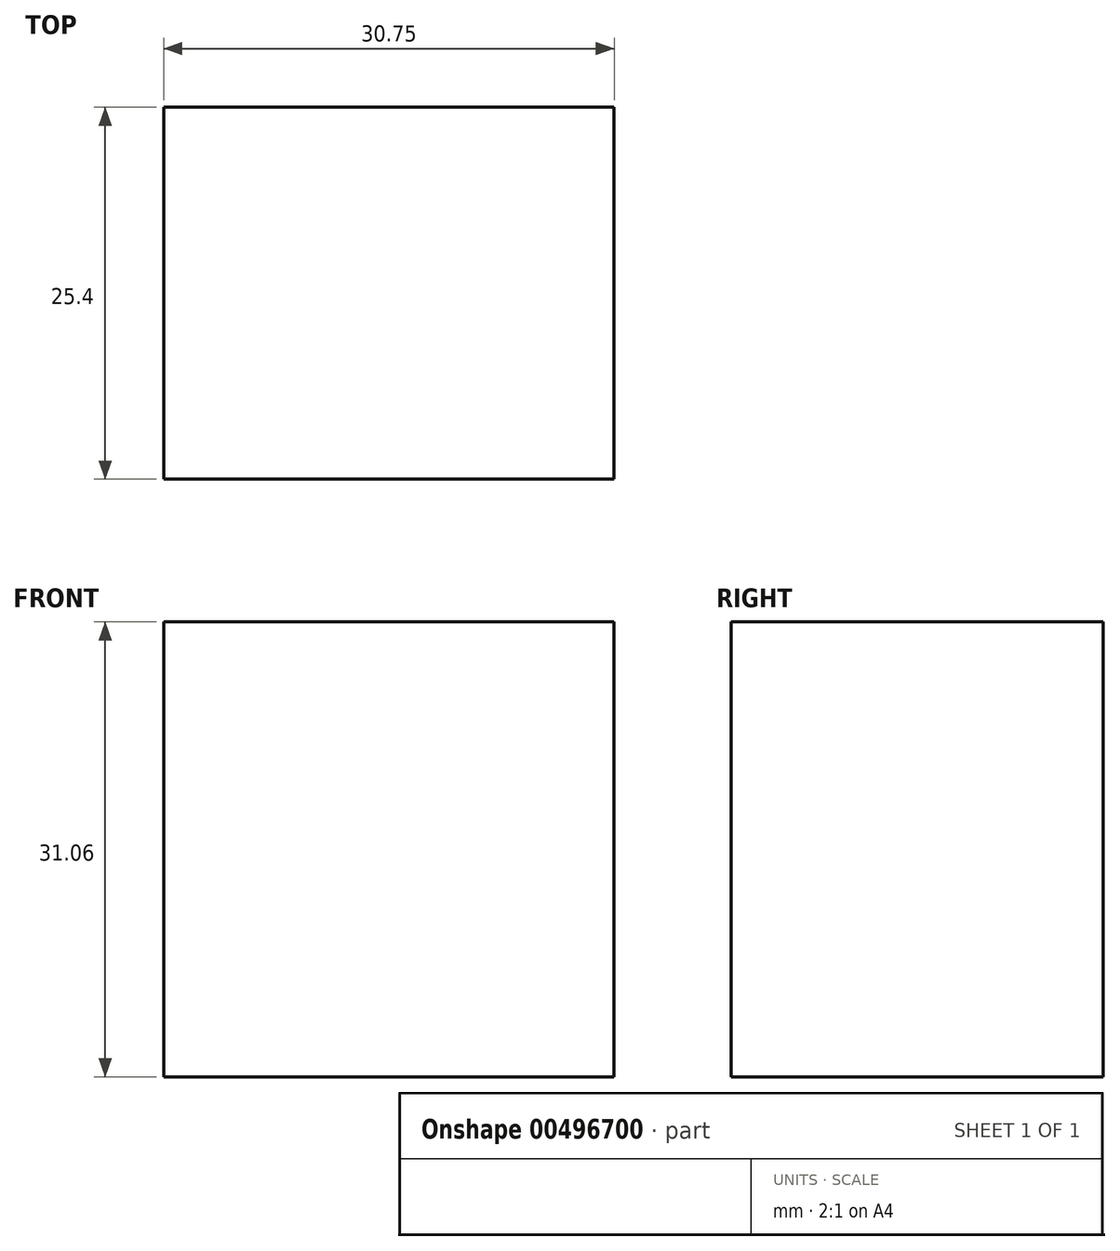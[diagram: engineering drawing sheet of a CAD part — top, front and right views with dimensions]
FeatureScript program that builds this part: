
annotation { "Feature Type Name" : "Feature", "Feature Type Description" : "" }
export const myFeature = defineFeature(function(context is Context, id is Id, definition is map)
    precondition{}
    {
        {
            var Q0;
            Q0=qCreatedBy(makeId("Front.planeOp"),FACE);
            var sketch = newSketch(context, id + "F0", { "sketchPlane" : qUnion([Q0])});
            skLineSegment(sketch, "E0.bottom", {"start": v(-14.6, 14.12) * mm, "end": v(16.16, 14.12) * mm});
            skLineSegment(sketch, "E0.top", {"start": v(-14.6, -16.94) * mm, "end": v(16.16, -16.94) * mm});
            skLineSegment(sketch, "E0.left", {"start": v(-14.6, 14.12) * mm, "end": v(-14.6, -16.94) * mm});
            skLineSegment(sketch, "E0.right", {"start": v(16.16, 14.12) * mm, "end": v(16.16, -16.94) * mm});
            skSolve(sketch);
        }
        {
            var Q0;
            Q0 = qSketchRegion(id + "F0", true);
            extrude(context, id + "F1", {"entities" : qUnion([Q0]), "depth" : 25.4 * mm, "offsetDistance" : 25.4 * mm});
        }
    });
